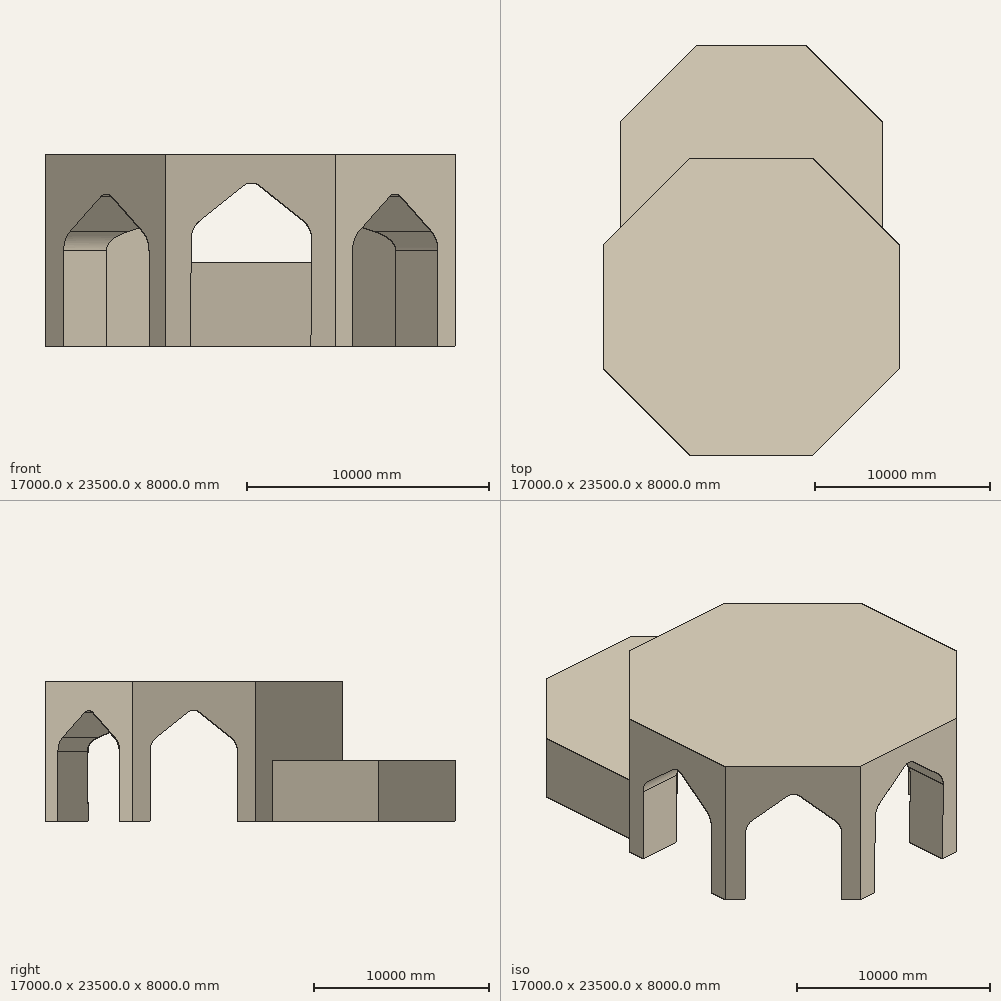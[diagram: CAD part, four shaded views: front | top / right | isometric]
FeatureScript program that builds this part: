
annotation { "Feature Type Name" : "Feature", "Feature Type Description" : "" }
export const myFeature = defineFeature(function(context is Context, id is Id, definition is map)
    precondition{}
    {
        {
            var Q0;
            Q0=qCreatedBy(makeId("Top.planeOp"),FACE);
            var sketch = newSketch(context, id + "F0", { "sketchPlane" : qUnion([Q0])});
            skLineSegment(sketch, "E0", {"start": v(0, 7500) * mm, "end": v(0, 0) * mm});
            skLineSegment(sketch, "E1", {"start": v(0, 0) * mm, "end": v(0, -8500) * mm});
            skCircle(sketch, "E2.cCircle", {"center": v(0, 7500) * mm, "radius": 7500 * mm, "construction": true});
            skLineSegment(sketch, "E2.0", {"start": v(3106.6, 0) * mm, "end": v(-3106.6, 0) * mm});
            skLineSegment(sketch, "E2.1", {"start": v(-3106.6, 0) * mm, "end": v(-7500, 4393.4) * mm});
            skLineSegment(sketch, "E2.2", {"start": v(-7500, 4393.4) * mm, "end": v(-7500, 10606.6) * mm});
            skLineSegment(sketch, "E2.3", {"start": v(-7500, 10606.6) * mm, "end": v(-3106.6, 15000) * mm});
            skLineSegment(sketch, "E2.4", {"start": v(-3106.6, 15000) * mm, "end": v(3106.6, 15000) * mm});
            skLineSegment(sketch, "E2.5", {"start": v(3106.6, 15000) * mm, "end": v(7500, 10606.6) * mm});
            skLineSegment(sketch, "E2.6", {"start": v(7500, 10606.6) * mm, "end": v(7500, 4393.4) * mm});
            skLineSegment(sketch, "E2.7", {"start": v(7500, 4393.4) * mm, "end": v(3106.6, 0) * mm});
            skPoint(sketch, "E2.0.midPoint", {"position": v(0, 0) * mm});
            skCircle(sketch, "E3.cCircle", {"center": v(0, 0) * mm, "radius": 8500 * mm, "construction": true});
            skLineSegment(sketch, "E3.0", {"start": v(3520.82, -8500) * mm, "end": v(-3520.82, -8500) * mm});
            skLineSegment(sketch, "E3.1", {"start": v(-3520.82, -8500) * mm, "end": v(-8500, -3520.82) * mm});
            skLineSegment(sketch, "E3.2", {"start": v(-8500, -3520.82) * mm, "end": v(-8500, 3520.82) * mm});
            skLineSegment(sketch, "E3.3", {"start": v(-8500, 3520.82) * mm, "end": v(-3520.82, 8500) * mm});
            skLineSegment(sketch, "E3.4", {"start": v(-3520.82, 8500) * mm, "end": v(3520.82, 8500) * mm});
            skLineSegment(sketch, "E3.5", {"start": v(3520.82, 8500) * mm, "end": v(8500, 3520.82) * mm});
            skLineSegment(sketch, "E3.6", {"start": v(8500, 3520.82) * mm, "end": v(8500, -3520.82) * mm});
            skLineSegment(sketch, "E3.7", {"start": v(8500, -3520.82) * mm, "end": v(3520.82, -8500) * mm});
            skPoint(sketch, "E3.0.midPoint", {"position": v(0, -8500) * mm});
            skSolve(sketch);
        }
        {
            var Q0;
            {var subQ1=sQuery(id+"F0.wireOp",EDGE,"E2.1");Q0=makeQuery(id+"F0.imprint","IMPRINT",FACE,{"disambiguationData":[TD([[makeQuery(id+"F0.imprint","IMPRINT",EDGE,{"derivedFrom":subQ1}),-1.0]])]});}
            var Q1;
            {var subQ5=sQuery(id+"F0.wireOp",EDGE,"E1");Q1=makeQuery(id+"F0.imprint","IMPRINT",FACE,{"disambiguationData":[TD([[makeQuery(id+"F0.imprint","IMPRINT",EDGE,{"derivedFrom":subQ5}),1.0]])]});}
            var Q2;
            {var subQ5=sQuery(id+"F0.wireOp",EDGE,"E1");Q2=makeQuery(id+"F0.imprint","IMPRINT",FACE,{"disambiguationData":[TD([[makeQuery(id+"F0.imprint","IMPRINT",EDGE,{"derivedFrom":subQ5}),-1.0]])]});}
            extrude(context, id + "F1", {"entities" : qUnion([Q0, Q1, Q2]), "depth" : 8000 * mm});
        }
        {
            var Q0;
            {var subQ2=sQuery(id+"F0.wireOp",EDGE,"E2.3");Q0=makeQuery(id+"F0.imprint","IMPRINT",FACE,{"disambiguationData":[TD([[makeQuery(id+"F0.imprint","IMPRINT",EDGE,{"derivedFrom":subQ2}),-1.0]])]});}
            extrude(context, id + "F2", {"entities" : qUnion([Q0]), "operationType" : NewBodyOperationType.ADD, "depth" : 3500 * mm});
        }
        {
            var Q0;
            Q0=makeQuery(id+"F1.opExtrude","SWEPT_FACE",FACE,{"disambiguationData":[OSD([sQuery(id+"F0.wireOp",EDGE,"E3.2")])]});
            var sketch = newSketch(context, id + "F3", { "sketchPlane" : qUnion([Q0])});
            skLineSegment(sketch, "E4", {"start": v(0, 0) * mm, "end": v(-2500, 0) * mm});
            skLineSegment(sketch, "E5", {"start": v(0, 0) * mm, "end": v(2500, 0) * mm});
            skLineSegment(sketch, "E6", {"start": v(-2500, 0) * mm, "end": v(-2500, 4019.38) * mm});
            skLineSegment(sketch, "E7", {"start": v(-2124.7, 4800.24) * mm, "end": v(-312.35, 6250.12) * mm});
            skLineSegment(sketch, "E8", {"start": v(312.35, 6250.12) * mm, "end": v(2124.7, 4800.24) * mm});
            skLineSegment(sketch, "E9", {"start": v(2500, 4019.38) * mm, "end": v(2500, 0) * mm});
            skPoint(sketch, "E10.visualSharp", {"position": v(-2500, 4500) * mm});
            skArc(sketch, "E10.filletArc", {"start": v(-2498.12, 4501.5) * mm, "mid": v(-2499.5, 4499.76) * mm, "end": v(-2500, 4497.6) * mm});
            skArc(sketch, "E11.filletArc", {"start": v(-2124.7, 4800.24) * mm, "mid": v(-2401.3, 4452.56) * mm, "end": v(-2500, 4019.38) * mm});
            skPoint(sketch, "E12.visualSharp", {"position": v(2500, 4500) * mm});
            skArc(sketch, "E12.filletArc", {"start": v(2500, 4019.38) * mm, "mid": v(2401.3, 4452.56) * mm, "end": v(2124.7, 4800.24) * mm});
            skPoint(sketch, "E13.visualSharp", {"position": v(0, 6500) * mm});
            skArc(sketch, "E13.filletArc", {"start": v(312.35, 6250.12) * mm, "mid": v(0, 6359.69) * mm, "end": v(-312.35, 6250.12) * mm});
            skSolve(sketch);
        }
        {
            var Q0;
            Q0=makeQuery(id+"F3.imprint","IMPRINT",FACE,{"disambiguationData":[TD([[makeQuery(id+"F3.imprint","IMPRINT",EDGE,{"derivedFrom":sQuery(id+"F3.wireOp",EDGE,"E4")}),-1.0]])]});
            extrude(context, id + "F4", {"entities" : qUnion([Q0]), "operationType" : NewBodyOperationType.REMOVE, "oppositeDirection" : true, "depth" : 17000 * mm});
        }
        {
            var Q0;
            Q0=makeQuery(id+"F1.opExtrude","SWEPT_FACE",FACE,{"disambiguationData":[OSD([sQuery(id+"F0.wireOp",EDGE,"E3.1")])]});
            var sketch = newSketch(context, id + "F5", { "sketchPlane" : qUnion([Q0])});
            skSolve(sketch);
        }
        {
            var Q0;
            {var subQ0=sQuery(id+"F0.wireOp",EDGE,"E3.1");Q0=makeQuery(id+"F5.imprint","IMPRINT",FACE,{"disambiguationData":[TD([[makeQuery(id+"F5.imprint","IMPRINT",EDGE,{"derivedFrom":makeQuery(id+"F1.opExtrude","CAP_EDGE",EDGE,{"disambiguationData":[OSD([subQ0])],"isStart":true})}),-1.0]])]});}
            var sketch = newSketch(context, id + "F6", { "sketchPlane" : qUnion([Q0])});
            skLineSegment(sketch, "E14", {"start": v(49.38, -24.93) * mm, "end": v(-2450.62, -24.93) * mm});
            skLineSegment(sketch, "E15", {"start": v(49.38, -24.93) * mm, "end": v(2549.38, -24.93) * mm});
            skLineSegment(sketch, "E16", {"start": v(-2450.62, -24.93) * mm, "end": v(-2450.62, 3994.44) * mm});
            skLineSegment(sketch, "E17", {"start": v(-2075.31, 4775.31) * mm, "end": v(-262.97, 6225.2) * mm});
            skLineSegment(sketch, "E18", {"start": v(361.73, 6225.2) * mm, "end": v(2174.08, 4775.31) * mm});
            skLineSegment(sketch, "E19", {"start": v(2549.38, 3994.44) * mm, "end": v(2549.38, -24.93) * mm});
            skArc(sketch, "E20.filletArc", {"start": v(-2075.31, 4775.31) * mm, "mid": v(-2351.92, 4427.63) * mm, "end": v(-2450.62, 3994.44) * mm});
            skArc(sketch, "E21.filletArc", {"start": v(2549.38, 3994.44) * mm, "mid": v(2450.68, 4427.63) * mm, "end": v(2174.08, 4775.31) * mm});
            skArc(sketch, "E22.filletArc", {"start": v(361.73, 6225.2) * mm, "mid": v(49.38, 6334.76) * mm, "end": v(-262.97, 6225.2) * mm});
            skLineSegment(sketch, "E23", {"start": v(0, 0) * mm, "end": v(0, -899.93) * mm});
            skSolve(sketch);
        }
        {
            var Q0;
            Q0=makeQuery(id+"F6.imprint","IMPRINT",FACE,{"disambiguationData":[TD([[makeQuery(id+"F6.imprint","IMPRINT",EDGE,{"derivedFrom":sQuery(id+"F6.wireOp",EDGE,"E17")}),-1.0]])]});
            extrude(context, id + "F7", {"entities" : qUnion([Q0]), "operationType" : NewBodyOperationType.REMOVE, "oppositeDirection" : true, "depth" : 16000 * mm});
        }
        {
            var Q0;
            Q0=makeQuery(id+"F1.opExtrude","SWEPT_FACE",FACE,{"disambiguationData":[OSD([sQuery(id+"F0.wireOp",EDGE,"E3.0")])]});
            var sketch = newSketch(context, id + "F8", { "sketchPlane" : qUnion([Q0])});
            skLineSegment(sketch, "E24", {"start": v(0, -1146.8) * mm, "end": v(0, 0) * mm});
            skLineSegment(sketch, "E25", {"start": v(4.02, -0.45) * mm, "end": v(-2495.98, -0.45) * mm});
            skLineSegment(sketch, "E26", {"start": v(4.02, -0.45) * mm, "end": v(2504.02, -0.45) * mm});
            skLineSegment(sketch, "E27", {"start": v(-2495.98, -0.45) * mm, "end": v(-2453.66, 4465.22) * mm});
            skLineSegment(sketch, "E28", {"start": v(-2078.4, 5236.6) * mm, "end": v(-266.05, 6686.49) * mm});
            skLineSegment(sketch, "E29", {"start": v(358.64, 6686.49) * mm, "end": v(2171, 5236.6) * mm});
            skLineSegment(sketch, "E30", {"start": v(2546.25, 4446.24) * mm, "end": v(2504.02, -0.45) * mm});
            skArc(sketch, "E31.filletArc", {"start": v(-2078.4, 5236.6) * mm, "mid": v(-2352.94, 4893.2) * mm, "end": v(-2453.66, 4465.22) * mm});
            skArc(sketch, "E32.filletArc", {"start": v(2546.25, 4446.24) * mm, "mid": v(2449.65, 4884.65) * mm, "end": v(2171, 5236.6) * mm});
            skArc(sketch, "E33.filletArc", {"start": v(358.64, 6686.49) * mm, "mid": v(46.3, 6796.05) * mm, "end": v(-266.05, 6686.49) * mm});
            skSolve(sketch);
        }
        {
            var Q0;
            Q0=makeQuery(id+"F8.imprint","IMPRINT",FACE,{"disambiguationData":[TD([[makeQuery(id+"F8.imprint","IMPRINT",EDGE,{"derivedFrom":sQuery(id+"F8.wireOp",EDGE,"E28")}),-1.0]])]});
            extrude(context, id + "F9", {"entities" : qUnion([Q0]), "operationType" : NewBodyOperationType.REMOVE, "oppositeDirection" : true, "depth" : 17000 * mm});
        }
        {
            var Q0;
            Q0=makeQuery(id+"F1.opExtrude","SWEPT_FACE",FACE,{"disambiguationData":[OSD([sQuery(id+"F0.wireOp",EDGE,"E3.7")])]});
            var sketch = newSketch(context, id + "F10", { "sketchPlane" : qUnion([Q0])});
            skLineSegment(sketch, "E34", {"start": v(0, -1341.91) * mm, "end": v(0, 0) * mm});
            skLineSegment(sketch, "E35", {"start": v(-10.33, -17.92) * mm, "end": v(-2510.33, -17.92) * mm});
            skLineSegment(sketch, "E36", {"start": v(-10.33, -17.92) * mm, "end": v(2489.67, -17.92) * mm});
            skLineSegment(sketch, "E37", {"start": v(-2510.33, -17.92) * mm, "end": v(-2510.33, 4001.46) * mm});
            skLineSegment(sketch, "E38", {"start": v(-2135.03, 4782.33) * mm, "end": v(-322.68, 6232.2) * mm});
            skLineSegment(sketch, "E39", {"start": v(302.02, 6232.2) * mm, "end": v(2114.36, 4782.33) * mm});
            skLineSegment(sketch, "E40", {"start": v(2489.67, 4001.46) * mm, "end": v(2489.67, -17.92) * mm});
            skArc(sketch, "E41.filletArc", {"start": v(-2135.03, 4782.33) * mm, "mid": v(-2411.64, 4434.65) * mm, "end": v(-2510.33, 4001.46) * mm});
            skArc(sketch, "E42.filletArc", {"start": v(2489.67, 4001.46) * mm, "mid": v(2390.97, 4434.65) * mm, "end": v(2114.36, 4782.33) * mm});
            skArc(sketch, "E43.filletArc", {"start": v(302.02, 6232.2) * mm, "mid": v(-10.33, 6341.77) * mm, "end": v(-322.68, 6232.2) * mm});
            skSolve(sketch);
        }
        {
            var Q0;
            Q0=makeQuery(id+"F10.imprint","IMPRINT",FACE,{"disambiguationData":[TD([[makeQuery(id+"F10.imprint","IMPRINT",EDGE,{"derivedFrom":sQuery(id+"F10.wireOp",EDGE,"E38")}),-1.0]])]});
            extrude(context, id + "F11", {"entities" : qUnion([Q0]), "operationType" : NewBodyOperationType.REMOVE, "oppositeDirection" : true, "depth" : 16000 * mm});
        }
    });
